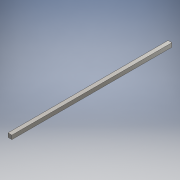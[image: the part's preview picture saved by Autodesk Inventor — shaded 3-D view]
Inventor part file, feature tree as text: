
AUTODESK INVENTOR PART (.ipt)
format: ipt  version: 2016 (Build 200138000, 138)  size: 90,112 bytes
history: native  units: mm
features: extrude x1, sketch x1
ambient origin geometry x8: Origin, YZ Plane, XZ Plane, XY Plane, X Axis, Y Axis, Z Axis, Center Point
bodies: Solid1 (feature_tree)
feature tree (2):
  extrude  "Extrusion1"  Depth=200.0mm
  sketch  "Sketch1"  dims[d0=8240.0mm d1=200.0mm d2=200.0mm d3=0.0mm]
